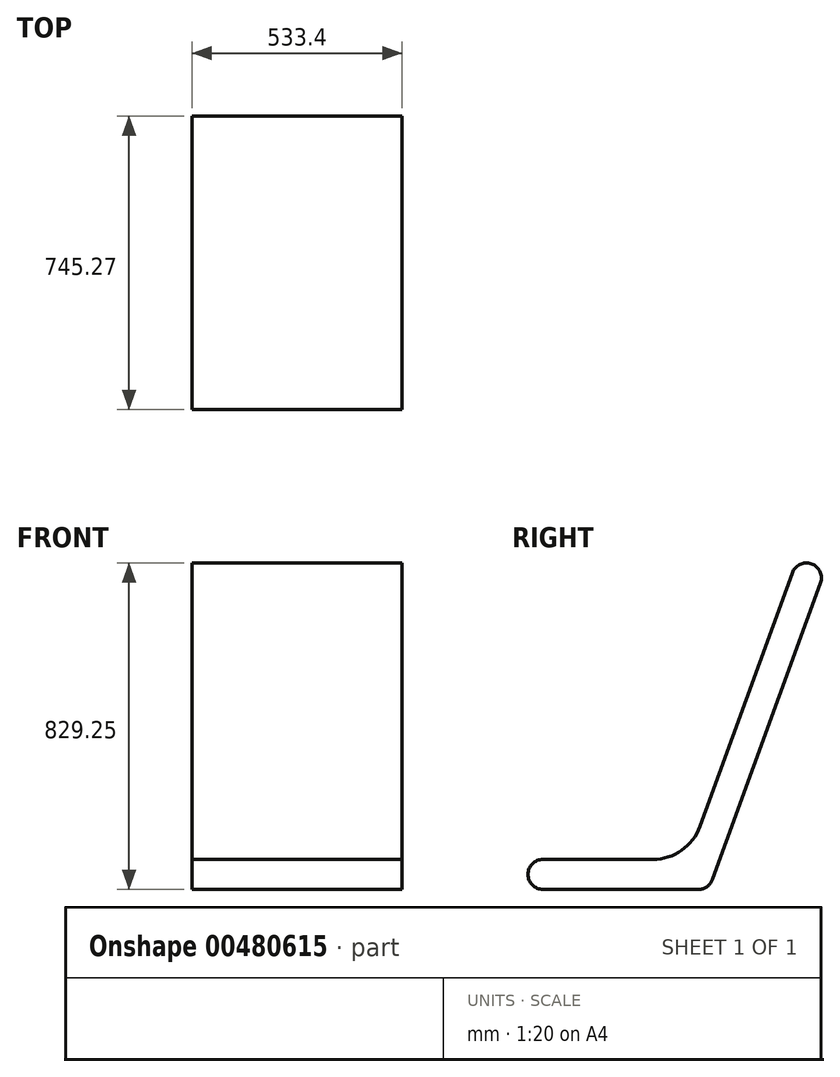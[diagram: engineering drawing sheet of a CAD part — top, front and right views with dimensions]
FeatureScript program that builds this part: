
annotation { "Feature Type Name" : "Feature", "Feature Type Description" : "" }
export const myFeature = defineFeature(function(context is Context, id is Id, definition is map)
    precondition{}
    {
        {
            var Q0;
            Q0=qCreatedBy(makeId("Right.planeOp"),FACE);
            var sketch = newSketch(context, id + "F0", { "sketchPlane" : qUnion([Q0])});
            skPoint(sketch, "E0.middle", {"position": v(0, 0) * mm});
            skLineSegment(sketch, "E1", {"start": v(1278.58, 2642.4) * mm, "end": v(714.52, 2642.4) * mm});
            skLineSegment(sketch, "E2", {"start": v(30.41, 83.56) * mm, "end": v(264.96, 727.98) * mm});
            skLineSegment(sketch, "E3", {"start": v(-88.93, 0) * mm, "end": v(-368.3, 0) * mm});
            skLineSegment(sketch, "E4.0", {"start": v(62.48, -51.13) * mm, "end": v(336.57, 701.92) * mm});
            skLineSegment(sketch, "E4.1", {"start": v(26.68, -76.2) * mm, "end": v(-368.3, -76.2) * mm});
            skArc(sketch, "E5.filletArc", {"start": v(-88.93, 0) * mm, "mid": v(-16.08, 22.97) * mm, "end": v(30.41, 83.56) * mm});
            skLineSegment(sketch, "E6", {"start": v(313.8, 750.75) * mm, "end": v(313.8, 750.75) * mm});
            skLineSegment(sketch, "E7", {"start": v(-406.4, -38.1) * mm, "end": v(-406.4, -38.1) * mm});
            skPoint(sketch, "E8.visualSharp", {"position": v(278, 763.78) * mm});
            skArc(sketch, "E8.filletArc", {"start": v(313.8, 750.75) * mm, "mid": v(284.66, 749.48) * mm, "end": v(264.96, 727.98) * mm});
            skPoint(sketch, "E9.visualSharp", {"position": v(349.6, 737.72) * mm});
            skArc(sketch, "E9.filletArc", {"start": v(336.57, 701.92) * mm, "mid": v(335.3, 731.05) * mm, "end": v(313.8, 750.75) * mm});
            skPoint(sketch, "E10.visualSharp", {"position": v(-406.4, 0) * mm});
            skArc(sketch, "E10.filletArc", {"start": v(-368.3, 0) * mm, "mid": v(-395.24, -11.16) * mm, "end": v(-406.4, -38.1) * mm});
            skPoint(sketch, "E11.visualSharp", {"position": v(-406.4, -76.2) * mm});
            skArc(sketch, "E11.filletArc", {"start": v(-406.4, -38.1) * mm, "mid": v(-395.24, -65.04) * mm, "end": v(-368.3, -76.2) * mm});
            skPoint(sketch, "E12.visualSharp", {"position": v(53.36, -76.2) * mm});
            skArc(sketch, "E12.filletArc", {"start": v(26.68, -76.2) * mm, "mid": v(48.53, -69.3) * mm, "end": v(62.48, -51.13) * mm});
            skSolve(sketch);
        }
        {
            var Q0;
            Q0 = qSketchRegion(id + "F0", true);
            extrude(context, id + "F1", {"entities" : qUnion([Q0]), "depth" : 533.4 * mm});
        }
    });
